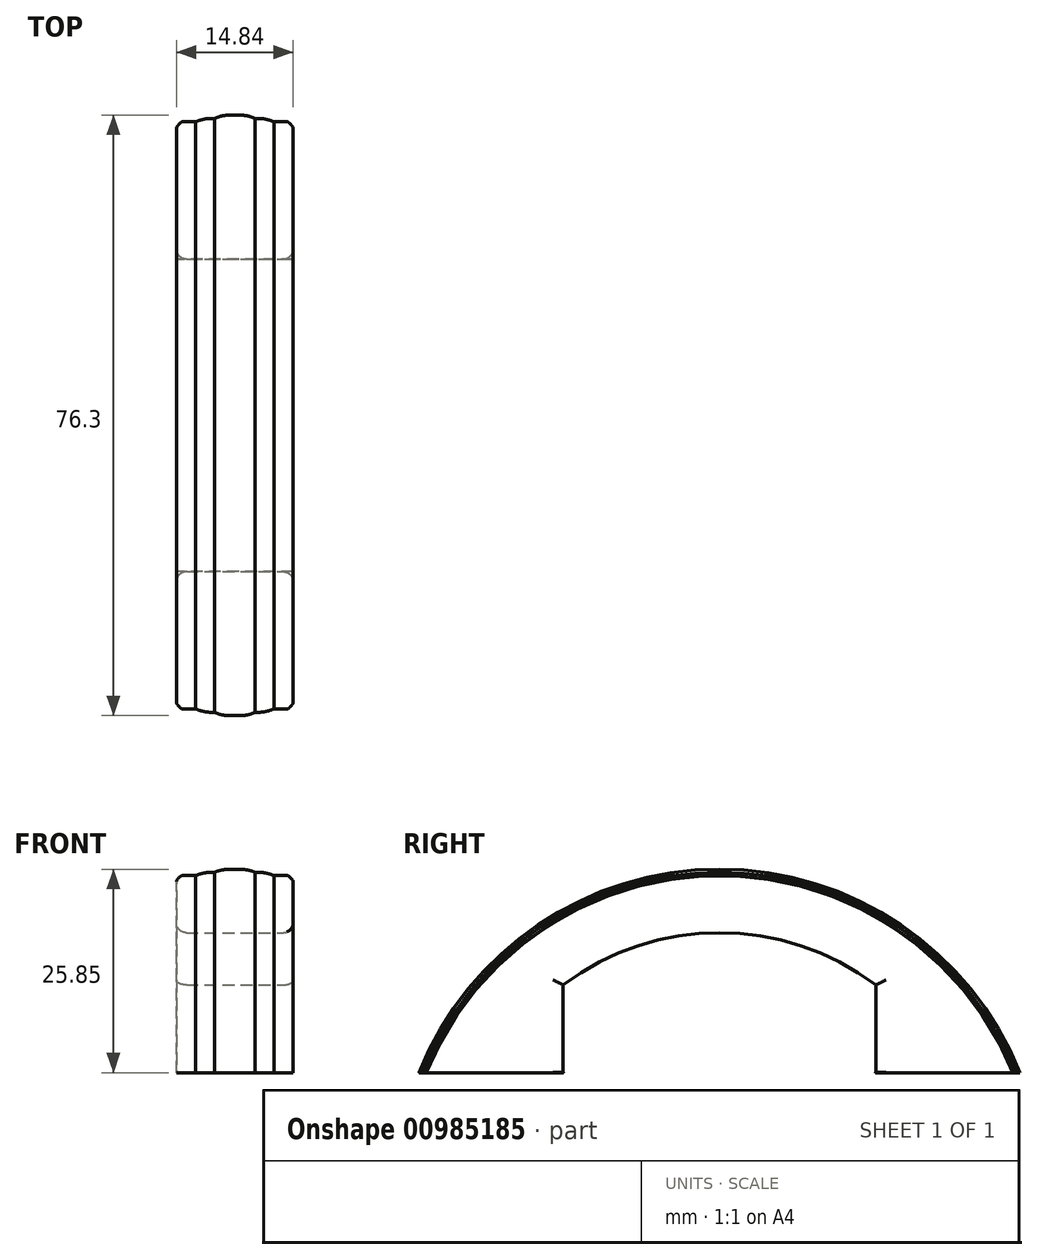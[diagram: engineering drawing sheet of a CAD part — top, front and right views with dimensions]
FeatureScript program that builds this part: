
annotation { "Feature Type Name" : "Feature", "Feature Type Description" : "" }
export const myFeature = defineFeature(function(context is Context, id is Id, definition is map)
    precondition{}
    {
        {
            var Q0;
            Q0=qCreatedBy(makeId("Front.planeOp"),FACE);
            var sketch = newSketch(context, id + "F0", { "sketchPlane" : qUnion([Q0])});
            skLineSegment(sketch, "E0", {"start": v(-55.67, 0) * mm, "end": v(68.03, 0) * mm, "construction": true});
            skLineSegment(sketch, "E1", {"start": v(-7.42, 0) * mm, "end": v(-7.42, 40.28) * mm});
            skLineSegment(sketch, "E2", {"start": v(-7.42, 40.28) * mm, "end": v(-4.96, 40.28) * mm});
            skLineSegment(sketch, "E3", {"start": v(-4.96, 40.28) * mm, "end": v(-4.96, 40.68) * mm});
            skLineSegment(sketch, "E4", {"start": v(-4.96, 40.68) * mm, "end": v(-2.58, 40.68) * mm});
            skLineSegment(sketch, "E5", {"start": v(-2.58, 40.68) * mm, "end": v(-2.58, 41.08) * mm});
            skLineSegment(sketch, "E6", {"start": v(-2.58, 41.08) * mm, "end": v(2.58, 41.08) * mm});
            skLineSegment(sketch, "E7", {"start": v(2.58, 41.08) * mm, "end": v(2.58, 40.68) * mm});
            skLineSegment(sketch, "E8", {"start": v(2.58, 40.68) * mm, "end": v(4.96, 40.68) * mm});
            skLineSegment(sketch, "E9", {"start": v(4.96, 40.68) * mm, "end": v(4.96, 40.28) * mm});
            skLineSegment(sketch, "E10", {"start": v(4.96, 40.28) * mm, "end": v(7.42, 40.28) * mm});
            skLineSegment(sketch, "E11", {"start": v(7.42, 40.28) * mm, "end": v(7.42, 0) * mm});
            skLineSegment(sketch, "E12", {"start": v(7.42, 0) * mm, "end": v(-7.42, 0) * mm});
            skLineSegment(sketch, "E13", {"start": v(0, 0) * mm, "end": v(0, 47.43) * mm, "construction": true});
            skSolve(sketch);
        }
        {
            var Q0;
            Q0=makeQuery(id+"F0.imprint","IMPRINT",FACE,{"disambiguationData":[TD([[makeQuery(id+"F0.imprint","IMPRINT",EDGE,{"derivedFrom":sQuery(id+"F0.wireOp",EDGE,"E1")}),-1.0]])]});
            var Q1;
            Q1=sQuery(id+"F0.wireOp",EDGE,"E0");
            revolve(context, id + "F1", {"surfaceOperationType" : NewSurfaceOperationType.NEW, "entities" : qUnion([Q0]), "axis" : qUnion([Q1]), "revolveType" : RevolveType.FULL});
        }
        {
            var Q0;
            Q0=makeQuery(id+"F1.opRevolve","SWEPT_EDGE",EDGE,{"disambiguationData":[OSD([sQuery(id+"F0.wireOp",EDGE,"E10"),sQuery(id+"F0.wireOp",EDGE,"E11")])]});
            var Q1;
            Q1=makeQuery(id+"F1.opRevolve","SWEPT_EDGE",EDGE,{"disambiguationData":[OSD([sQuery(id+"F0.wireOp",EDGE,"E1"),sQuery(id+"F0.wireOp",EDGE,"E2")])]});
            fillet(context, id + "F2", {"entities" : qUnion([Q0, Q1]), "radius" : 0.76 * mm, "tangentPropagation" : true, "rho" : 0.2, "crossSection" : FilletCrossSection.CONIC, "allowEdgeOverflow" : false});
        }
        {
            var Q0;
            Q0=makeQuery(id+"F1.opRevolve","SWEPT_EDGE",EDGE,{"disambiguationData":[OSD([sQuery(id+"F0.wireOp",EDGE,"E8"),sQuery(id+"F0.wireOp",EDGE,"E9")])]});
            var Q1;
            Q1=makeQuery(id+"F1.opRevolve","SWEPT_EDGE",EDGE,{"disambiguationData":[OSD([sQuery(id+"F0.wireOp",EDGE,"E3"),sQuery(id+"F0.wireOp",EDGE,"E4")])]});
            fillet(context, id + "F3", {"entities" : qUnion([Q0, Q1]), "radius" : 5.08 * mm, "tangentPropagation" : true, "allowEdgeOverflow" : false});
        }
        {
            var Q0;
            Q0=makeQuery(id+"F1.opRevolve","SWEPT_EDGE",EDGE,{"disambiguationData":[OSD([sQuery(id+"F0.wireOp",EDGE,"E6"),sQuery(id+"F0.wireOp",EDGE,"E7")])]});
            var Q1;
            Q1=makeQuery(id+"F1.opRevolve","SWEPT_EDGE",EDGE,{"disambiguationData":[OSD([sQuery(id+"F0.wireOp",EDGE,"E5"),sQuery(id+"F0.wireOp",EDGE,"E6")])]});
            fillet(context, id + "F4", {"entities" : qUnion([Q0, Q1]), "radius" : 5.08 * mm, "tangentPropagation" : true, "allowEdgeOverflow" : false});
        }
        {
            var Q0;
            Q0=qCreatedBy(makeId("Right.planeOp"),FACE);
            var sketch = newSketch(context, id + "F5", { "sketchPlane" : qUnion([Q0])});
            skCircle(sketch, "E14", {"center": v(0, 0) * mm, "radius": 25 * mm});
            skSolve(sketch);
        }
        {
            var Q0;
            Q0=qSketchRegion(id+"F5",true);
            extrude(context, id + "F6", {"entities" : qUnion([Q0]), "operationType" : NewBodyOperationType.REMOVE, "endBound" : BoundingType.THROUGH_ALL, "depth" : 25.4 * mm, "offsetDistance" : 25.4 * mm, "hasSecondDirection" : true, "secondDirectionBound" : SecondDirectionBoundingType.THROUGH_ALL, "secondDirectionOppositeDirection" : true, "secondDirectionDepth" : 25.4 * mm});
        }
        {
            var Q0;
            Q0=qCreatedBy(makeId("Right.planeOp"),FACE);
            var sketch = newSketch(context, id + "F7", { "sketchPlane" : qUnion([Q0])});
            skLineSegment(sketch, "E15", {"start": v(0, 15.23) * mm, "end": v(-38.1, 15.23) * mm, "construction": true});
            skLineSegment(sketch, "E16.MirrorCS", {"start": v(0, 15.23) * mm, "end": v(38.1, 15.23) * mm, "construction": true});
            skLineSegment(sketch, "E17", {"start": v(-59.25, 15.23) * mm, "end": v(65.7, 15.23) * mm});
            skLineSegment(sketch, "E18", {"start": v(65.7, 15.23) * mm, "end": v(65.7, -43.9) * mm});
            skLineSegment(sketch, "E19", {"start": v(65.7, -43.9) * mm, "end": v(-59.25, -43.9) * mm});
            skLineSegment(sketch, "E20", {"start": v(-59.25, -43.9) * mm, "end": v(-59.25, 15.23) * mm});
            skSolve(sketch);
        }
        {
            var Q0;
            Q0=qSketchRegion(id+"F7",true);
            extrude(context, id + "F8", {"entities" : qUnion([Q0]), "operationType" : NewBodyOperationType.REMOVE, "endBound" : BoundingType.THROUGH_ALL, "oppositeDirection" : true, "depth" : 25.4 * mm, "offsetDistance" : 25.4 * mm, "hasSecondDirection" : true, "secondDirectionBound" : SecondDirectionBoundingType.THROUGH_ALL, "secondDirectionOppositeDirection" : false, "secondDirectionDepth" : 25.4 * mm});
        }
        {
            var Q0;
            Q0=qCreatedBy(makeId("Right.planeOp"),FACE);
            var sketch = newSketch(context, id + "F9", { "sketchPlane" : qUnion([Q0])});
            skLineSegment(sketch, "E21", {"start": v(-19.86, 15.26) * mm, "end": v(-19.86, 26.38) * mm});
            skLineSegment(sketch, "E22.MirrorCS", {"start": v(19.86, 15.26) * mm, "end": v(19.86, 26.38) * mm});
            skArc(sketch, "E23", {"start": v(-19.86, 26.38) * mm, "mid": v(0, 33.01) * mm, "end": v(19.86, 26.38) * mm});
            skLineSegment(sketch, "E24", {"start": v(-19.86, 15.26) * mm, "end": v(19.86, 15.26) * mm});
            skSolve(sketch);
        }
        {
            var Q0;
            Q0=qSketchRegion(id+"F9",true);
            extrude(context, id + "F10", {"entities" : qUnion([Q0]), "operationType" : NewBodyOperationType.REMOVE, "endBound" : BoundingType.THROUGH_ALL, "oppositeDirection" : true, "depth" : 25.4 * mm, "offsetDistance" : 25.4 * mm, "hasSecondDirection" : true, "secondDirectionBound" : SecondDirectionBoundingType.THROUGH_ALL, "secondDirectionOppositeDirection" : false, "secondDirectionDepth" : 25.4 * mm});
        }
        {
            var Q0;
            Q0=makeQuery(id+"F10.boolean.opBoolean","INTERSECT",EDGE,{"derivedFrom":[makeQuery(id+"F1.opRevolve","SWEPT_FACE",FACE,{"disambiguationData":[OSD([sQuery(id+"F0.wireOp",EDGE,"E11")])]}),makeQuery(id+"F10.opExtrude","SWEPT_FACE",FACE,{"disambiguationData":[OSD([sQuery(id+"F9.wireOp",EDGE,"E23")])]})]});
            var Q1;
            Q1=makeQuery(id+"F10.boolean.opBoolean","INTERSECT",EDGE,{"derivedFrom":[makeQuery(id+"F1.opRevolve","SWEPT_FACE",FACE,{"disambiguationData":[OSD([sQuery(id+"F0.wireOp",EDGE,"E11")])]}),makeQuery(id+"F10.opExtrude","SWEPT_FACE",FACE,{"disambiguationData":[OSD([sQuery(id+"F9.wireOp",EDGE,"E21")])]})]});
            var Q2;
            Q2=makeQuery(id+"F10.boolean.opBoolean","INTERSECT",EDGE,{"derivedFrom":[makeQuery(id+"F1.opRevolve","SWEPT_FACE",FACE,{"disambiguationData":[OSD([sQuery(id+"F0.wireOp",EDGE,"E11")])]}),makeQuery(id+"F10.opExtrude","SWEPT_FACE",FACE,{"disambiguationData":[OSD([sQuery(id+"F9.wireOp",EDGE,"E22.MirrorCS")])]})]});
            var Q3;
            Q3=makeQuery(id+"F10.boolean.opBoolean","INTERSECT",EDGE,{"derivedFrom":[makeQuery(id+"F1.opRevolve","SWEPT_FACE",FACE,{"disambiguationData":[OSD([sQuery(id+"F0.wireOp",EDGE,"E1")])]}),makeQuery(id+"F10.opExtrude","SWEPT_FACE",FACE,{"disambiguationData":[OSD([sQuery(id+"F9.wireOp",EDGE,"E23")])]})]});
            var Q4;
            Q4=makeQuery(id+"F10.boolean.opBoolean","INTERSECT",EDGE,{"derivedFrom":[makeQuery(id+"F1.opRevolve","SWEPT_FACE",FACE,{"disambiguationData":[OSD([sQuery(id+"F0.wireOp",EDGE,"E1")])]}),makeQuery(id+"F10.opExtrude","SWEPT_FACE",FACE,{"disambiguationData":[OSD([sQuery(id+"F9.wireOp",EDGE,"E21")])]})]});
            var Q5;
            Q5=makeQuery(id+"F10.boolean.opBoolean","INTERSECT",EDGE,{"derivedFrom":[makeQuery(id+"F1.opRevolve","SWEPT_FACE",FACE,{"disambiguationData":[OSD([sQuery(id+"F0.wireOp",EDGE,"E1")])]}),makeQuery(id+"F10.opExtrude","SWEPT_FACE",FACE,{"disambiguationData":[OSD([sQuery(id+"F9.wireOp",EDGE,"E22.MirrorCS")])]})]});
            fillet(context, id + "F11", {"entities" : qUnion([Q0, Q1, Q2, Q3, Q4, Q5]), "radius" : 1.27 * mm, "tangentPropagation" : true, "allowEdgeOverflow" : false});
        }
    });
